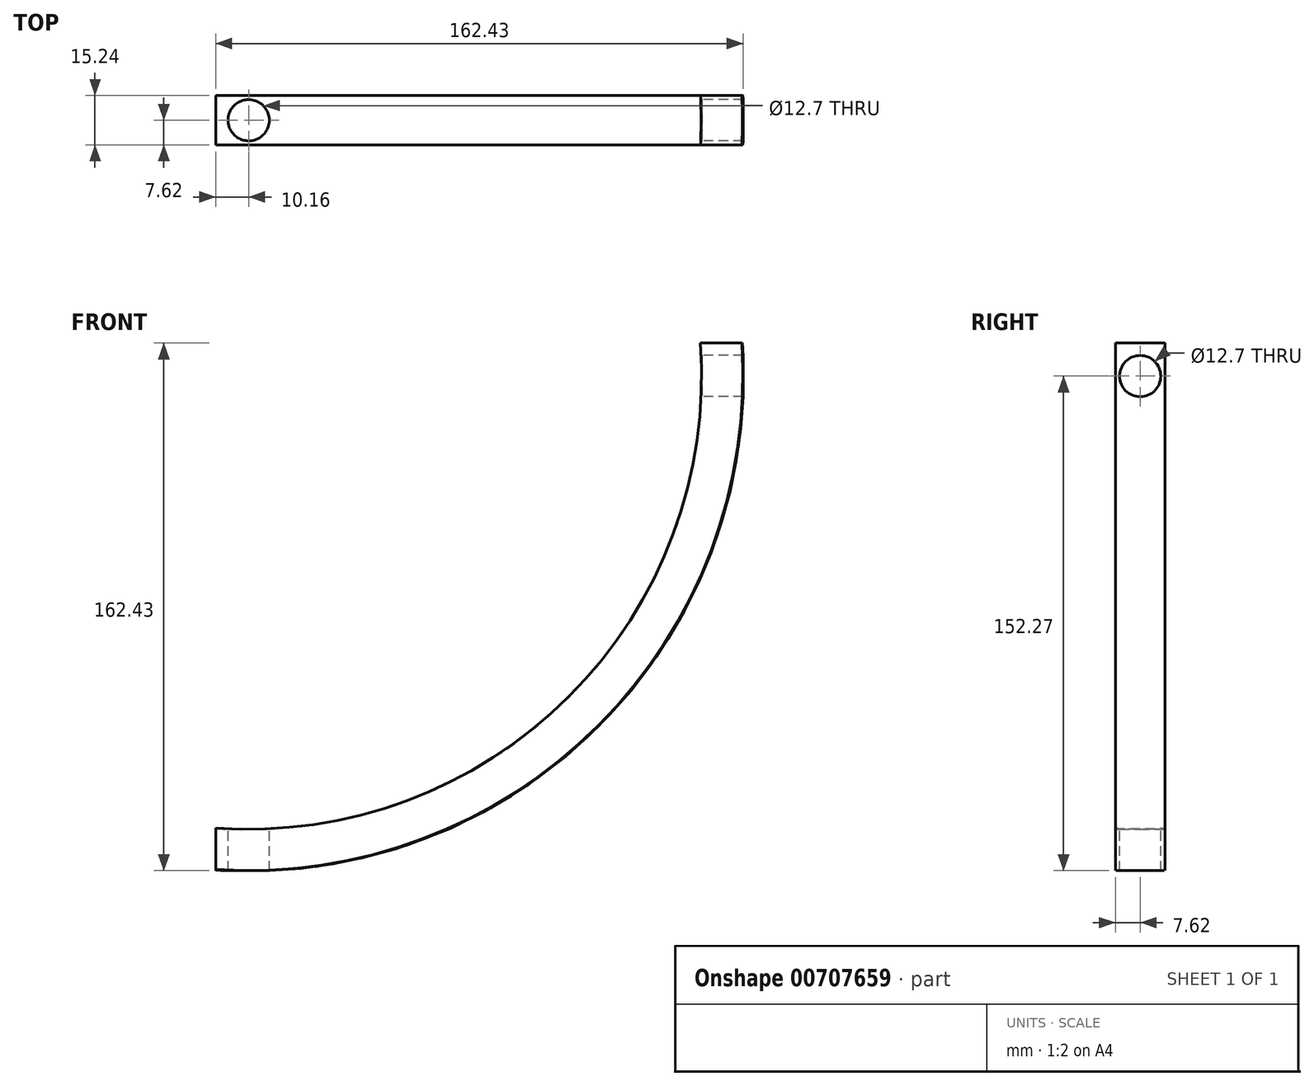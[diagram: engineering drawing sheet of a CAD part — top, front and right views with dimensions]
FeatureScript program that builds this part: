
annotation { "Feature Type Name" : "Feature", "Feature Type Description" : "" }
export const myFeature = defineFeature(function(context is Context, id is Id, definition is map)
    precondition{}
    {
        {
            var Q0;
            Q0=qCreatedBy(makeId("Front.planeOp"),FACE);
            var sketch = newSketch(context, id + "F0", { "sketchPlane" : qUnion([Q0])});
            skArc(sketch, "E0", {"start": v(0, -152.4) * mm, "mid": v(111.3, -104.1) * mm, "end": v(152.06, 10.16) * mm});
            skArc(sketch, "E1", {"start": v(0, -139.7) * mm, "mid": v(102.31, -95.12) * mm, "end": v(139.33, 10.16) * mm});
            skLineSegment(sketch, "E2", {"start": v(139.33, 10.16) * mm, "end": v(152.06, 10.16) * mm});
            skLineSegment(sketch, "E3", {"start": v(0, -139.7) * mm, "end": v(0, -152.4) * mm});
            skLineSegment(sketch, "E4", {"start": v(0, 98.78) * mm, "end": v(0, -95.1) * mm, "construction": true});
            skSolve(sketch);
        }
        {
            var Q0;
            Q0=makeQuery(id+"F0.imprint","IMPRINT",FACE,{"disambiguationData":[TD([[makeQuery(id+"F0.imprint","IMPRINT",EDGE,{"derivedFrom":sQuery(id+"F0.wireOp",EDGE,"E0")}),1.0]])]});
            var Q1;
            Q1=sQuery(id+"F0.wireOp",EDGE,"E4");
            revolve(context, id + "F1", {"surfaceOperationType" : NewSurfaceOperationType.NEW, "entities" : qUnion([Q0]), "axis" : qUnion([Q1]), "revolveType" : RevolveType.FULL});
        }
        {
            var Q0;
            Q0=qCreatedBy(makeId("Top.planeOp"),FACE);
            var sketch = newSketch(context, id + "F2", { "sketchPlane" : qUnion([Q0])});
            skLineSegment(sketch, "E5.bottom", {"start": v(-205.86, 180.99) * mm, "end": v(247.88, 180.99) * mm});
            skLineSegment(sketch, "E5.top", {"start": v(-205.86, 7.62) * mm, "end": v(247.88, 7.62) * mm});
            skLineSegment(sketch, "E5.left", {"start": v(-205.86, 180.99) * mm, "end": v(-205.86, 7.62) * mm});
            skLineSegment(sketch, "E5.right", {"start": v(247.88, 180.99) * mm, "end": v(247.88, 7.62) * mm});
            skLineSegment(sketch, "E6.bottom", {"start": v(-199.04, -7.62) * mm, "end": v(230.97, -7.62) * mm});
            skLineSegment(sketch, "E6.top", {"start": v(-199.04, -208.82) * mm, "end": v(230.97, -208.82) * mm});
            skLineSegment(sketch, "E6.left", {"start": v(-199.04, -7.62) * mm, "end": v(-199.04, -208.82) * mm});
            skLineSegment(sketch, "E6.right", {"start": v(230.97, -7.62) * mm, "end": v(230.97, -208.82) * mm});
            skSolve(sketch);
        }
        {
            var Q0;
            Q0=makeQuery(id+"F2.imprint","IMPRINT",FACE,{"disambiguationData":[TD([[makeQuery(id+"F2.imprint","IMPRINT",EDGE,{"derivedFrom":sQuery(id+"F2.wireOp",EDGE,"E5.bottom")}),-1.0]])]});
            var Q1;
            Q1=makeQuery(id+"F2.imprint","IMPRINT",FACE,{"disambiguationData":[TD([[makeQuery(id+"F2.imprint","IMPRINT",EDGE,{"derivedFrom":sQuery(id+"F2.wireOp",EDGE,"E6.bottom")}),-1.0]])]});
            extrude(context, id + "F3", {"entities" : qUnion([Q0, Q1]), "operationType" : NewBodyOperationType.REMOVE, "endBound" : BoundingType.SYMMETRIC, "oppositeDirection" : true, "depth" : 418.6 * mm, "offsetDistance" : 25.4 * mm});
        }
        {
            var Q0;
            Q0=qCreatedBy(makeId("Front.planeOp"),FACE);
            var sketch = newSketch(context, id + "F4", { "sketchPlane" : qUnion([Q0])});
            skLineSegment(sketch, "E7.bottom", {"start": v(-10.16, 221.16) * mm, "end": v(-321.68, 221.16) * mm});
            skLineSegment(sketch, "E7.top", {"start": v(-10.16, -265.33) * mm, "end": v(-321.68, -265.33) * mm});
            skLineSegment(sketch, "E7.left", {"start": v(-10.16, 221.16) * mm, "end": v(-10.16, -265.33) * mm});
            skLineSegment(sketch, "E7.right", {"start": v(-321.68, 221.16) * mm, "end": v(-321.68, -265.33) * mm});
            skSolve(sketch);
        }
        {
            var Q0;
            Q0=makeQuery(id+"F4.imprint","IMPRINT",FACE,{"disambiguationData":[TD([[makeQuery(id+"F4.imprint","IMPRINT",EDGE,{"derivedFrom":sQuery(id+"F4.wireOp",EDGE,"E7.bottom")}),1.0]])]});
            extrude(context, id + "F5", {"entities" : qUnion([Q0]), "operationType" : NewBodyOperationType.REMOVE, "endBound" : BoundingType.SYMMETRIC, "depth" : 97.54 * mm, "offsetDistance" : 25.4 * mm});
        }
        {
            var Q0;
            Q0=qCreatedBy(makeId("Right.planeOp"),FACE);
            var sketch = newSketch(context, id + "F6", { "sketchPlane" : qUnion([Q0])});
            skCircle(sketch, "E8", {"center": v(0, 0) * mm, "radius": 6.35 * mm});
            skSolve(sketch);
        }
        {
            var Q0;
            Q0 = qSketchRegion(id + "F6", true);
            extrude(context, id + "F7", {"entities" : qUnion([Q0]), "operationType" : NewBodyOperationType.REMOVE, "depth" : 281.94 * mm, "offsetDistance" : 25.4 * mm});
        }
        {
            var Q0;
            Q0=qCreatedBy(makeId("Top.planeOp"),FACE);
            var sketch = newSketch(context, id + "F8", { "sketchPlane" : qUnion([Q0])});
            skCircle(sketch, "E9", {"center": v(0, 0) * mm, "radius": 6.35 * mm});
            skSolve(sketch);
        }
        {
            var Q0;
            Q0 = qSketchRegion(id + "F8", true);
            extrude(context, id + "F9", {"entities" : qUnion([Q0]), "operationType" : NewBodyOperationType.REMOVE, "oppositeDirection" : true, "depth" : 203.2 * mm, "offsetDistance" : 25.4 * mm});
        }
    });
